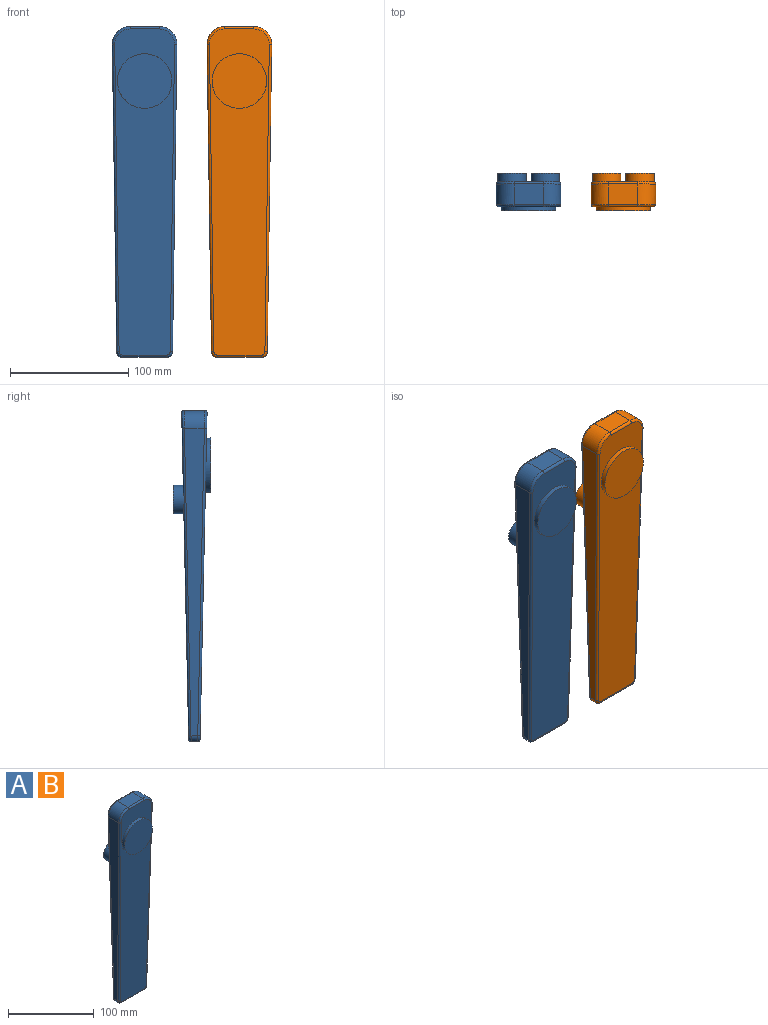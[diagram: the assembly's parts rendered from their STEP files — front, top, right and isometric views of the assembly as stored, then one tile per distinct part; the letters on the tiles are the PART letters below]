
ASSEMBLY  parts=2 mates=1
PART A: 32 faces, bbox 54.6x32x279.4 mm
  f0: cylinder r=2mm len=259.28mm, axis (0.01,0.02,1), area 800.7mm2, adj f6,f7,f26,f27,f30
  f1: cylinder r=2mm len=259.28mm, axis (0.01,-0.02,-1), area 800.7mm2, adj f4,f7,f22,f23,f28
  f2: plane 37.14x5.59mm, normal (0,0,-1), area 207.4mm2, adj f12,f13,f17,f24
  f3: plane 24.57x17.41mm, normal (0,0,1), area 427.8mm2, adj f10,f11,f18,f25
  f4: plane 259.26x16.85mm, normal (-1,0,-0.01), area 2924.6mm2, adj f1,f11,f13,f14
  f5: plane 275.4x50.57mm, normal (0,-1,-0.02), area 11205.6mm2, adj f8,f14,f15,f16,f17,f18,f19,f20
  f6: plane 259.26x16.85mm, normal (1,0,-0.01), area 2924.6mm2, adj f0,f10,f12,f21
  f7: plane 275.4x50.57mm, normal (0,1,-0.02), area 11988.2mm2, adj f0,f1,f22,f23,f24,f25,f26,f27
  f8: cylinder r=23mm len=46mm, axis (0,1,0), area 612.4mm2, adj f5,f9
  f9: plane 46x46mm, normal (0,-1,0), area 1661.9mm2, adj f8
  f10: cylinder r=15mm len=17.41mm, axis (0,-1,0), area 409.1mm2, adj f3,f6,f20,f27
  f11: cylinder r=15mm len=17.41mm, axis (0,-1,0), area 409.1mm2, adj f3,f4,f16,f23
  f12: cylinder r=5mm len=5.71mm, axis (0,1,0), area 44mm2, adj f2,f6,f19,f26
  f13: cylinder r=5mm len=5.71mm, axis (0,1,0), area 44mm2, adj f2,f4,f15,f22
  f14: cylinder r=2mm len=259.28mm, axis (-0.01,-0.02,1), area 814.6mm2, adj f4,f5,f15,f16
  f15: bspline ~5.22x5mm, area 20.7mm2, adj f5,f13,f14,f17
  f16: bspline ~15.24x15mm, area 71.7mm2, adj f5,f11,f14,f18
  f17: cylinder r=2mm len=37.14mm, axis (-1,0,0), area 115.1mm2, adj f2,f5,f15,f19
  f18: cylinder r=2mm len=24.57mm, axis (1,0,0), area 78.2mm2, adj f3,f5,f16,f20
  f19: bspline ~5.22x5mm, area 20.7mm2, adj f5,f12,f17,f21
  f20: bspline ~15.24x15mm, area 71.7mm2, adj f5,f10,f18,f21
  f21: cylinder r=2mm len=259.28mm, axis (-0.01,0.02,-1), area 814.6mm2, adj f5,f6,f19,f20
  f22: bspline ~5.22x5.22mm, area 20.7mm2, adj f1,f7,f13,f24
  f23: bspline ~15.24x15mm, area 71.7mm2, adj f1,f7,f11,f25
  f24: cylinder r=2mm len=37.14mm, axis (-1,0,0), area 115.1mm2, adj f2,f7,f22,f26
  f25: cylinder r=2mm len=24.57mm, axis (1,0,0), area 78.2mm2, adj f3,f7,f23,f27
  f26: bspline ~5.87x5.22mm, area 20.7mm2, adj f0,f7,f12,f24
  f27: bspline ~15.24x15mm, area 71.7mm2, adj f0,f7,f10,f25
  f28: cylinder r=12mm len=24mm, axis (0,1,0), area 672.8mm2, adj f1,f7,f29
  f29: plane 24x24mm, normal (0,1,0), area 452.4mm2, adj f28
  f30: cylinder r=12mm len=24mm, axis (0,1,0), area 672.8mm2, adj f0,f7,f31
  f31: plane 24x24mm, normal (0,1,0), area 452.4mm2, adj f30
PART B: same geometry as A
PLACE A t=(2.76,65.74,-40.48)mm
PLACE B t=(82.76,65.74,-40.48)mm
MATE fastened B.f3 <-> A.f3  axis (0,0,1) through (82.76,65.74,238.92)mm
